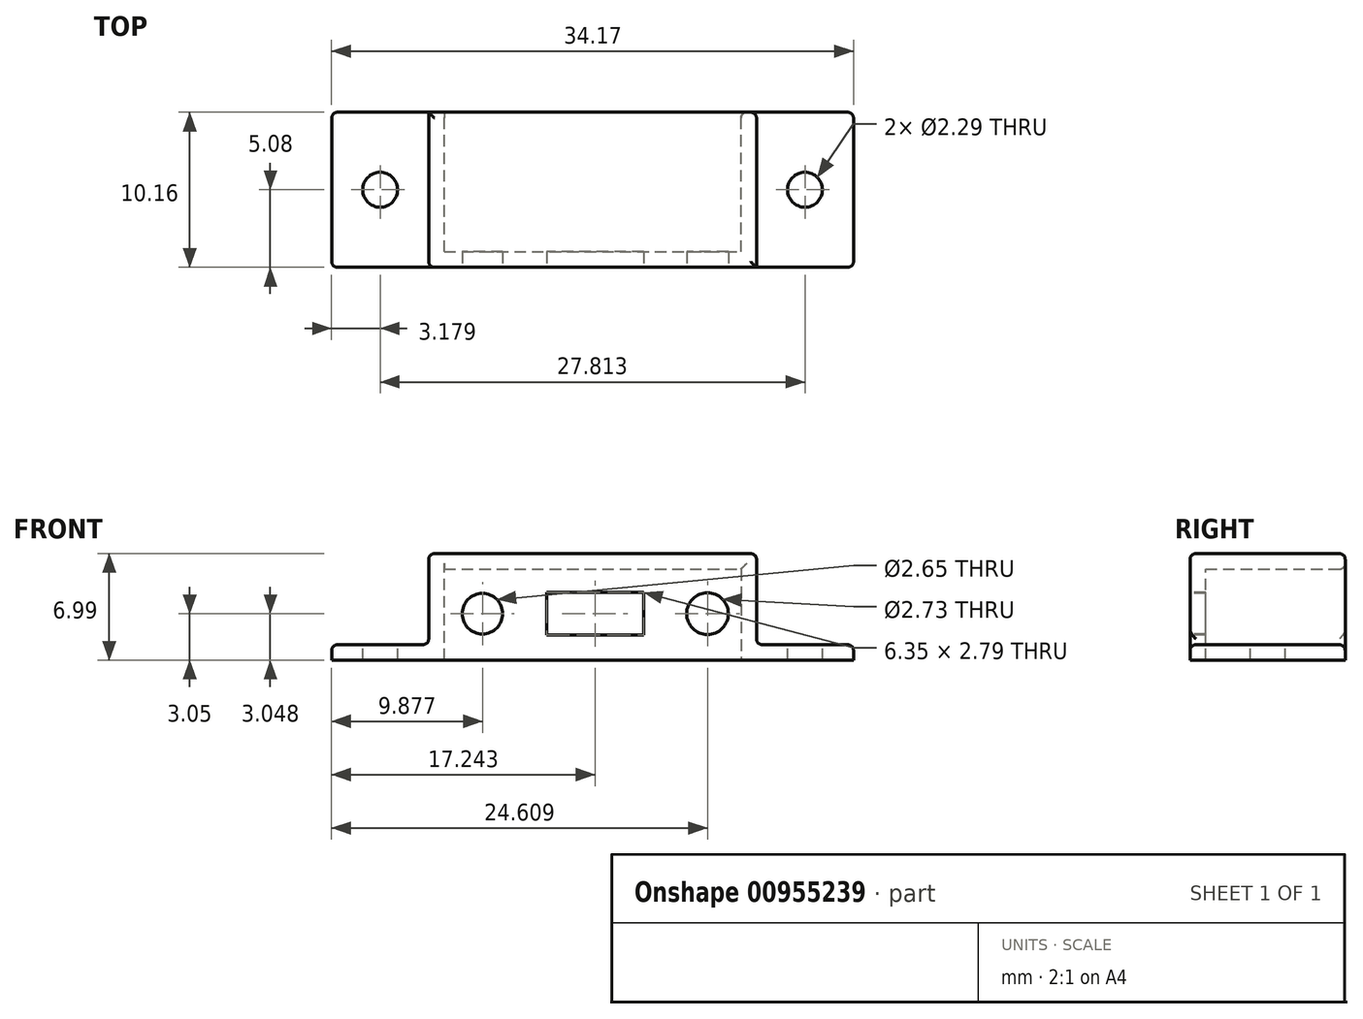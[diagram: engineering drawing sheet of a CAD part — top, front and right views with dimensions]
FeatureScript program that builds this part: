
annotation { "Feature Type Name" : "Feature", "Feature Type Description" : "" }
export const myFeature = defineFeature(function(context is Context, id is Id, definition is map)
    precondition{}
    {
        {
            var Q0;
            Q0=qCreatedBy(makeId("Front.planeOp"),FACE);
            var sketch = newSketch(context, id + "F0", { "sketchPlane" : qUnion([Q0])});
            skLineSegment(sketch, "E0", {"start": v(-7.37, 0) * mm, "end": v(0, 0) * mm});
            skLineSegment(sketch, "E1", {"start": v(0, 0) * mm, "end": v(0, 5.97) * mm});
            skLineSegment(sketch, "E2", {"start": v(0, 5.97) * mm, "end": v(19.43, 5.97) * mm});
            skLineSegment(sketch, "E3", {"start": v(19.43, 5.97) * mm, "end": v(19.43, 0) * mm});
            skLineSegment(sketch, "E4", {"start": v(19.43, 0) * mm, "end": v(26.8, 0) * mm});
            skLineSegment(sketch, "E5", {"start": v(26.8, 0) * mm, "end": v(26.8, 1.02) * mm});
            skLineSegment(sketch, "E6", {"start": v(26.8, 1.02) * mm, "end": v(20.45, 1.02) * mm});
            skLineSegment(sketch, "E7", {"start": v(20.45, 1.02) * mm, "end": v(20.45, 6.99) * mm});
            skLineSegment(sketch, "E8", {"start": v(20.45, 6.99) * mm, "end": v(-1.02, 6.99) * mm});
            skLineSegment(sketch, "E9", {"start": v(-1.02, 6.99) * mm, "end": v(-1.02, 1.02) * mm});
            skLineSegment(sketch, "E10", {"start": v(-1.02, 1.02) * mm, "end": v(-7.37, 1.02) * mm});
            skLineSegment(sketch, "E11", {"start": v(-7.37, 1.02) * mm, "end": v(-7.37, 0) * mm});
            skLineSegment(sketch, "E12.left", {"start": v(0, 5.97) * mm, "end": v(0, 0) * mm});
            skSolve(sketch);
        }
        {
            var Q0;
            Q0=makeQuery(id+"F0.imprint","IMPRINT",FACE,{"disambiguationData":[TD([[makeQuery(id+"F0.imprint","IMPRINT",EDGE,{"derivedFrom":sQuery(id+"F0.wireOp",EDGE,"E0")}),1.0]])]});
            extrude(context, id + "F1", {"entities" : qUnion([Q0]), "depth" : 10.16 * mm, "offsetDistance" : 25.4 * mm});
        }
        {
            var Q0;
            Q0=makeQuery(id+"F1.opExtrude","SWEPT_FACE",FACE,{"disambiguationData":[OSD([sQuery(id+"F0.wireOp",EDGE,"E10")])]});
            var sketch = newSketch(context, id + "F2", { "sketchPlane" : qUnion([Q0])});
            skCircle(sketch, "E13", {"center": v(-4.2, -5.08) * mm, "radius": 1.14 * mm});
            skPoint(sketch, "E13.centerSnap0", {"position": v(-7.37, -5.08) * mm});
            skCircle(sketch, "E14", {"center": v(23.62, -5.08) * mm, "radius": 1.1 * mm});
            skSolve(sketch);
        }
        {
            var Q0;
            Q0=sQuery(id+"F2.wireOp",VERTEX,"E13.center");
            var Q1;
            Q1=sQuery(id+"F2.wireOp",VERTEX,"E14.center");
            var Q2;
            Q2=makeQuery(id+"F1.opExtrude","SWEPT_BODY",BODY,{"disambiguationData":[OSD([sQuery(id+"F0.wireOp",EDGE,"E0"),sQuery(id+"F0.wireOp",EDGE,"E1"),sQuery(id+"F0.wireOp",EDGE,"E2"),sQuery(id+"F0.wireOp",EDGE,"E3"),sQuery(id+"F0.wireOp",EDGE,"E4"),sQuery(id+"F0.wireOp",EDGE,"E5"),sQuery(id+"F0.wireOp",EDGE,"E6"),sQuery(id+"F0.wireOp",EDGE,"E7"),sQuery(id+"F0.wireOp",EDGE,"E8"),sQuery(id+"F0.wireOp",EDGE,"E9"),sQuery(id+"F0.wireOp",EDGE,"E10"),sQuery(id+"F0.wireOp",EDGE,"E11")])]});
            hole(context, id + "F3", {"style" : HoleStyle.SIMPLE, "endStyle" : HoleEndStyle.THROUGH, "holeDiameter" : 2.3 * mm, "majorDiameter" : 6.35 * mm, "isTappedThrough" : true, "tappedDepth" : 12.7 * mm, "tapClearance" : 3, "locations" : qUnion([Q0, Q1]), "scope" : qUnion([Q2])});
        }
        {
            var Q0;
            Q0=makeQuery(id+"F1.opExtrude","CAP_FACE",FACE,{"disambiguationData":[OSD([sQuery(id+"F0.wireOp",EDGE,"E0"),sQuery(id+"F0.wireOp",EDGE,"E4"),sQuery(id+"F0.wireOp",EDGE,"E5"),sQuery(id+"F0.wireOp",EDGE,"E6"),sQuery(id+"F0.wireOp",EDGE,"E7"),sQuery(id+"F0.wireOp",EDGE,"E8"),sQuery(id+"F0.wireOp",EDGE,"E9"),sQuery(id+"F0.wireOp",EDGE,"E10"),sQuery(id+"F0.wireOp",EDGE,"E11"),sQuery(id+"F0.wireOp",EDGE,"E2"),sQuery(id+"F0.wireOp",EDGE,"E12.left"),sQuery(id+"F0.wireOp",EDGE,"E3")])],"isStart":false});
            var sketch = newSketch(context, id + "F4", { "sketchPlane" : qUnion([Q0])});
            skLineSegment(sketch, "E15.bottom", {"start": v(0, 0) * mm, "end": v(19.43, 0) * mm});
            skLineSegment(sketch, "E15.top", {"start": v(0, 5.97) * mm, "end": v(19.43, 5.97) * mm});
            skLineSegment(sketch, "E15.left", {"start": v(0, 0) * mm, "end": v(0, 5.97) * mm});
            skLineSegment(sketch, "E15.right", {"start": v(19.43, 0) * mm, "end": v(19.43, 5.97) * mm});
            skLineSegment(sketch, "E16.bottom", {"start": v(13.05, 1.65) * mm, "end": v(6.7, 1.65) * mm});
            skLineSegment(sketch, "E16.top", {"start": v(13.05, 4.45) * mm, "end": v(6.7, 4.45) * mm});
            skLineSegment(sketch, "E16.left", {"start": v(13.05, 1.65) * mm, "end": v(13.05, 4.45) * mm});
            skLineSegment(sketch, "E16.right", {"start": v(6.7, 1.65) * mm, "end": v(6.7, 4.45) * mm});
            skPoint(sketch, "E16.middle", {"position": v(9.87, 3.05) * mm});
            skCircle(sketch, "E17", {"center": v(2.5, 3.05) * mm, "radius": 1.33 * mm});
            skCircle(sketch, "E18", {"center": v(17.24, 3.05) * mm, "radius": 1.36 * mm});
            skSolve(sketch);
        }
        {
            var Q0;
            Q0=makeQuery(id+"F4.imprint","IMPRINT",FACE,{"disambiguationData":[TD([[makeQuery(id+"F4.imprint","IMPRINT",EDGE,{"derivedFrom":sQuery(id+"F4.wireOp",EDGE,"E15.bottom")}),1.0]])]});
            extrude(context, id + "F5", {"entities" : qUnion([Q0]), "operationType" : NewBodyOperationType.ADD, "depth" : -1.02 * mm, "offsetDistance" : 25.4 * mm});
        }
        {
            var Q0;
            Q0=makeQuery(id+"F1.opExtrude","SWEPT_FACE",FACE,{"disambiguationData":[OSD([sQuery(id+"F0.wireOp",EDGE,"E8")])]});
            var Q1;
            Q1=makeQuery(id+"F1.opExtrude","CAP_EDGE",EDGE,{"disambiguationData":[OSD([sQuery(id+"F0.wireOp",EDGE,"E9")])],"isStart":false});
            var Q2;
            Q2=makeQuery(id+"F1.opExtrude","SWEPT_EDGE",EDGE,{"disambiguationData":[OSD([sQuery(id+"F0.wireOp",EDGE,"E9"),sQuery(id+"F0.wireOp",EDGE,"E10")])]});
            var Q3;
            Q3=makeQuery(id+"F1.opExtrude","CAP_EDGE",EDGE,{"disambiguationData":[OSD([sQuery(id+"F0.wireOp",EDGE,"E10")])],"isStart":false});
            var Q4;
            Q4=makeQuery(id+"F1.opExtrude","CAP_EDGE",EDGE,{"disambiguationData":[OSD([sQuery(id+"F0.wireOp",EDGE,"E11")])],"isStart":false});
            var Q5;
            Q5=makeQuery(id+"F1.opExtrude","SWEPT_EDGE",EDGE,{"disambiguationData":[OSD([sQuery(id+"F0.wireOp",EDGE,"E10"),sQuery(id+"F0.wireOp",EDGE,"E11")])]});
            var Q6;
            Q6=makeQuery(id+"F1.opExtrude","CAP_EDGE",EDGE,{"disambiguationData":[OSD([sQuery(id+"F0.wireOp",EDGE,"E11")])],"isStart":true});
            var Q7;
            Q7=makeQuery(id+"F1.opExtrude","CAP_EDGE",EDGE,{"disambiguationData":[OSD([sQuery(id+"F0.wireOp",EDGE,"E10")])],"isStart":true});
            var Q8;
            Q8=makeQuery(id+"F1.opExtrude","CAP_EDGE",EDGE,{"disambiguationData":[OSD([sQuery(id+"F0.wireOp",EDGE,"E12.left")])],"isStart":true});
            var Q9;
            Q9=makeQuery(id+"F1.opExtrude","CAP_EDGE",EDGE,{"disambiguationData":[OSD([sQuery(id+"F0.wireOp",EDGE,"E2")])],"isStart":true});
            var Q10;
            Q10=makeQuery(id+"F1.opExtrude","CAP_EDGE",EDGE,{"disambiguationData":[OSD([sQuery(id+"F0.wireOp",EDGE,"E3")])],"isStart":true});
            var Q11;
            Q11=makeQuery(id+"F1.opExtrude","CAP_EDGE",EDGE,{"disambiguationData":[OSD([sQuery(id+"F0.wireOp",EDGE,"E7")])],"isStart":true});
            var Q12;
            Q12=makeQuery(id+"F1.opExtrude","SWEPT_EDGE",EDGE,{"disambiguationData":[OSD([sQuery(id+"F0.wireOp",EDGE,"E6"),sQuery(id+"F0.wireOp",EDGE,"E7")])]});
            var Q13;
            Q13=makeQuery(id+"F1.opExtrude","CAP_EDGE",EDGE,{"disambiguationData":[OSD([sQuery(id+"F0.wireOp",EDGE,"E6")])],"isStart":true});
            var Q14;
            Q14=makeQuery(id+"F1.opExtrude","CAP_EDGE",EDGE,{"disambiguationData":[OSD([sQuery(id+"F0.wireOp",EDGE,"E5")])],"isStart":true});
            var Q15;
            Q15=makeQuery(id+"F1.opExtrude","SWEPT_EDGE",EDGE,{"disambiguationData":[OSD([sQuery(id+"F0.wireOp",EDGE,"E5"),sQuery(id+"F0.wireOp",EDGE,"E6")])]});
            var Q16;
            Q16=makeQuery(id+"F1.opExtrude","CAP_EDGE",EDGE,{"disambiguationData":[OSD([sQuery(id+"F0.wireOp",EDGE,"E5")])],"isStart":false});
            var Q17;
            Q17=makeQuery(id+"F1.opExtrude","CAP_EDGE",EDGE,{"disambiguationData":[OSD([sQuery(id+"F0.wireOp",EDGE,"E6")])],"isStart":false});
            fillet(context, id + "F6", {"entities" : qUnion([Q0, Q1, Q2, Q3, Q4, Q5, Q6, Q7, Q8, Q9, Q10, Q11, Q12, Q13, Q14, Q15, Q16, Q17]), "radius" : 0.38 * mm, "tangentPropagation" : true, "allowEdgeOverflow" : false});
        }
    });
